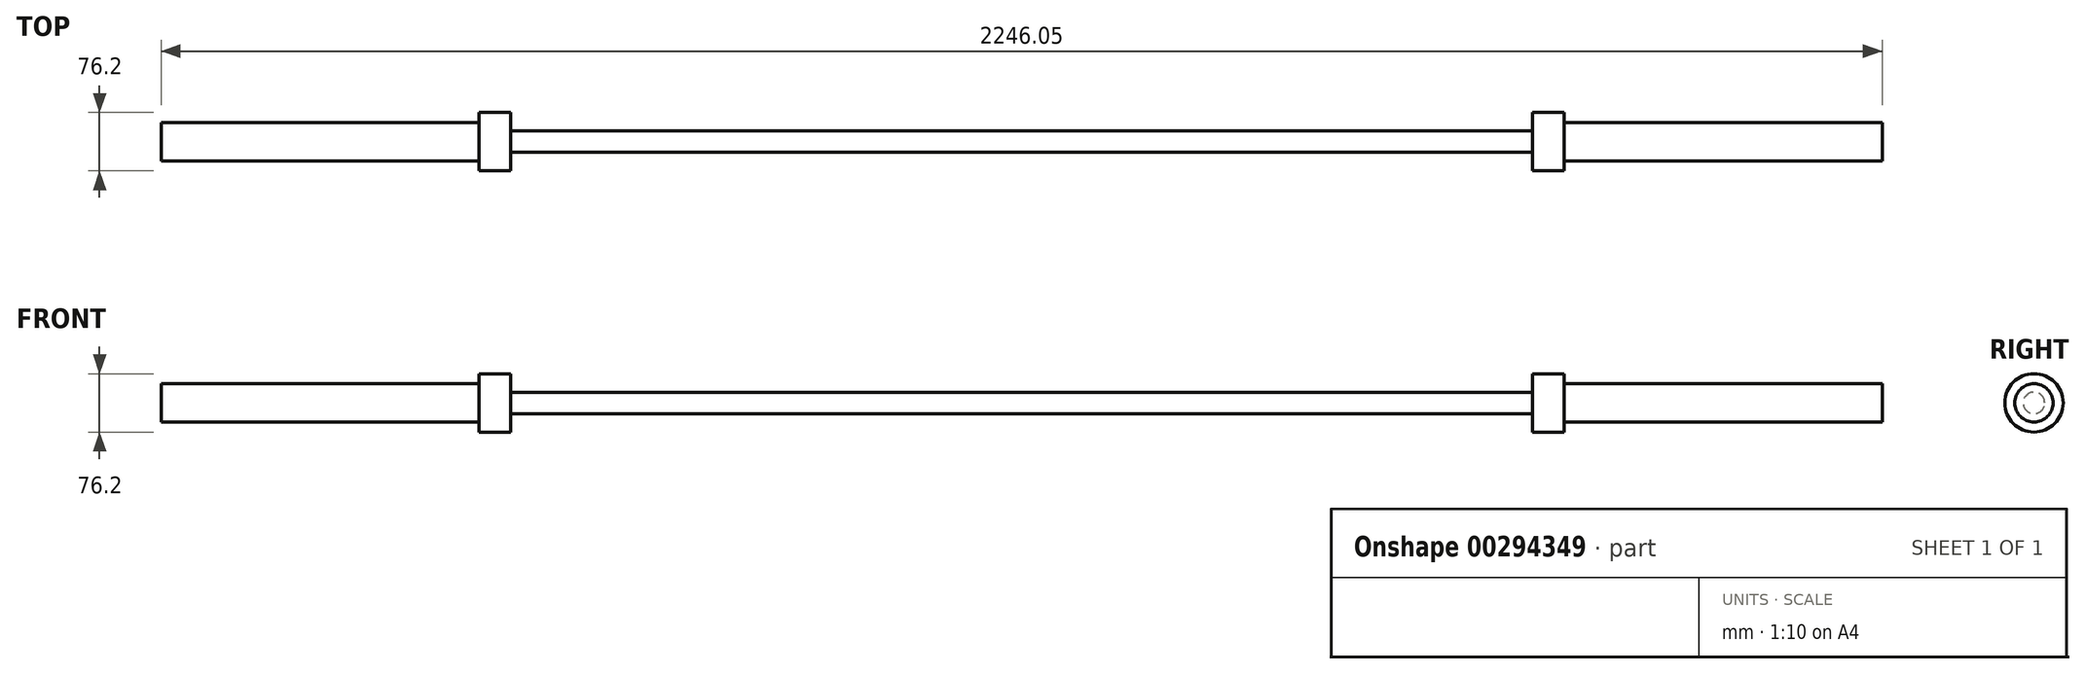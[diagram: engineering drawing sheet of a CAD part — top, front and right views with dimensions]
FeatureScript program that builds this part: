
annotation { "Feature Type Name" : "Feature", "Feature Type Description" : "" }
export const myFeature = defineFeature(function(context is Context, id is Id, definition is map)
    precondition{}
    {
        {
            var Q0;
            Q0=qCreatedBy(makeId("Right.planeOp"),FACE);
            var sketch = newSketch(context, id + "F0", { "sketchPlane" : qUnion([Q0])});
            skCircle(sketch, "E0", {"center": v(0, 0) * mm, "radius": 25 * mm});
            skSolve(sketch);
        }
        {
            var Q0;
            Q0 = qSketchRegion(id + "F0", true);
            extrude(context, id + "F1", {"entities" : qUnion([Q0]), "oppositeDirection" : true, "depth" : 415 * mm});
        }
        {
            var Q0;
            Q0=makeQuery(id+"F1.opExtrude","CAP_FACE",FACE,{"disambiguationData":[OSD([sQuery(id+"F0.wireOp",EDGE,"E0")])],"isStart":false});
            var sketch = newSketch(context, id + "F2", { "sketchPlane" : qUnion([Q0])});
            skCircle(sketch, "E1", {"center": v(0, 0) * mm, "radius": 38.1 * mm});
            skSolve(sketch);
        }
        {
            var Q0;
            Q0 = qSketchRegion(id + "F2", true);
            extrude(context, id + "F3", {"entities" : qUnion([Q0]), "operationType" : NewBodyOperationType.ADD, "depth" : 41.27 * mm});
        }
        {
            var Q0;
            Q0=makeQuery(id+"F3.opExtrude","CAP_FACE",FACE,{"disambiguationData":[OSD([sQuery(id+"F2.wireOp",EDGE,"E1")])],"isStart":false});
            var sketch = newSketch(context, id + "F4", { "sketchPlane" : qUnion([Q0])});
            skCircle(sketch, "E2", {"center": v(0, 0) * mm, "radius": 14 * mm});
            skSolve(sketch);
        }
        {
            var Q0;
            Q0 = qSketchRegion(id + "F4", true);
            extrude(context, id + "F5", {"entities" : qUnion([Q0]), "operationType" : NewBodyOperationType.ADD, "depth" : 1333.5 * mm});
        }
        {
            var Q0;
            Q0=makeQuery(id+"F5.opExtrude","CAP_FACE",FACE,{"disambiguationData":[OSD([sQuery(id+"F4.wireOp",EDGE,"E2")])],"isStart":false});
            var sketch = newSketch(context, id + "F6", { "sketchPlane" : qUnion([Q0])});
            skCircle(sketch, "E3", {"center": v(0, 0) * mm, "radius": 38.1 * mm});
            skSolve(sketch);
        }
        {
            var Q0;
            Q0 = qSketchRegion(id + "F6", true);
            extrude(context, id + "F7", {"entities" : qUnion([Q0]), "operationType" : NewBodyOperationType.ADD, "depth" : 41.27 * mm});
        }
        {
            var Q0;
            Q0=makeQuery(id+"F7.opExtrude","CAP_FACE",FACE,{"disambiguationData":[OSD([sQuery(id+"F6.wireOp",EDGE,"E3")])],"isStart":false});
            var sketch = newSketch(context, id + "F8", { "sketchPlane" : qUnion([Q0])});
            skCircle(sketch, "E4", {"center": v(0, 0) * mm, "radius": 25 * mm});
            skSolve(sketch);
        }
        {
            var Q0;
            Q0 = qSketchRegion(id + "F8", true);
            extrude(context, id + "F9", {"entities" : qUnion([Q0]), "operationType" : NewBodyOperationType.ADD, "depth" : 415 * mm});
        }
    });
